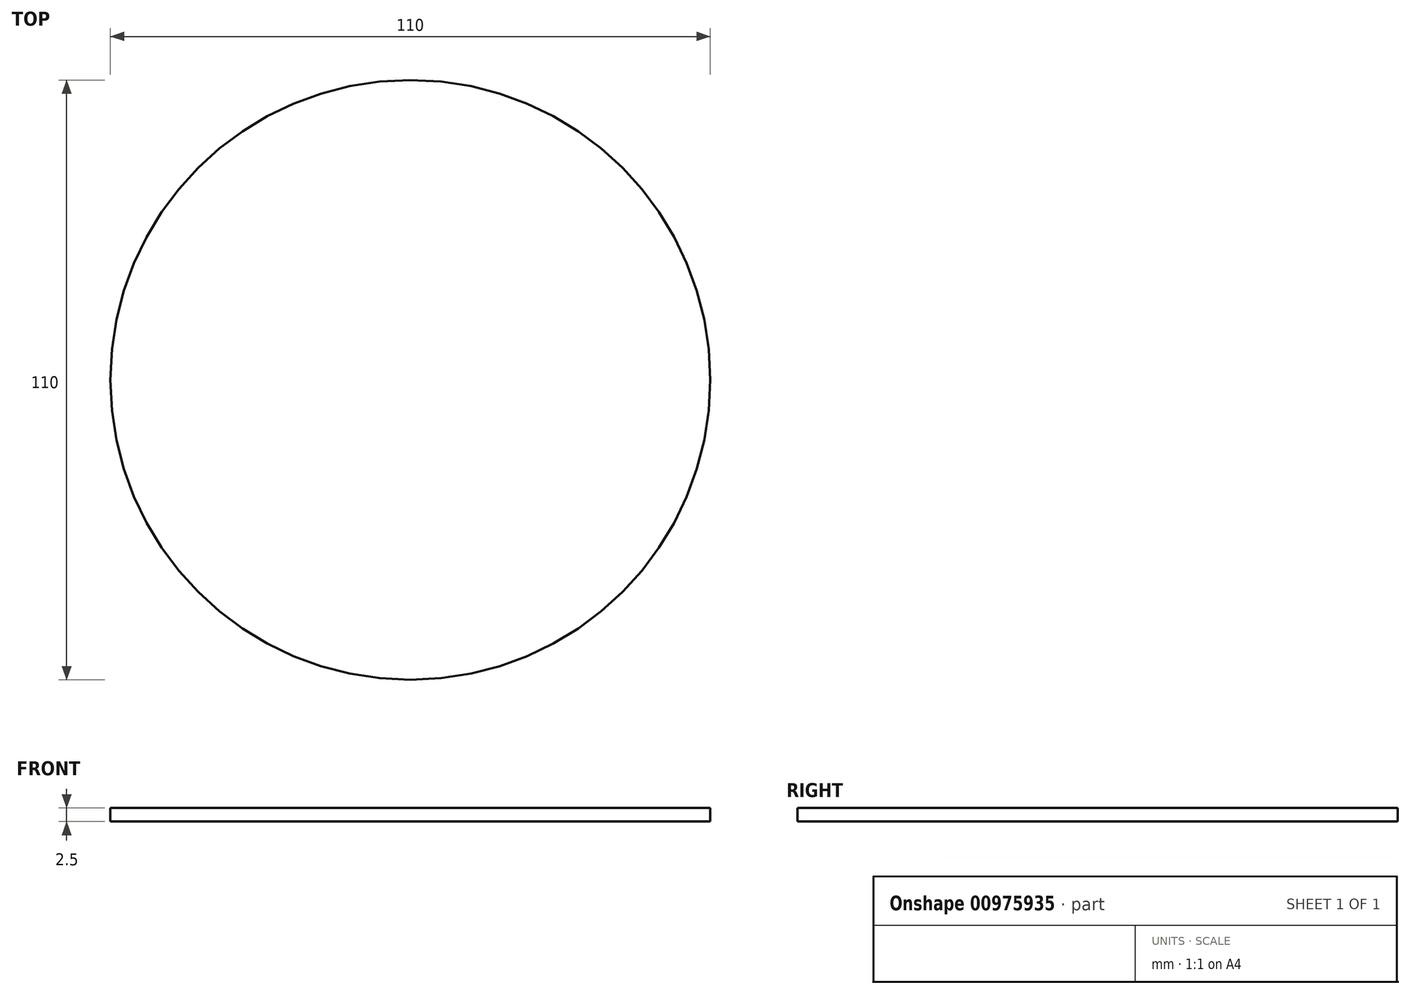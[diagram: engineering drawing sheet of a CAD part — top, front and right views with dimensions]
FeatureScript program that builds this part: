
annotation { "Feature Type Name" : "Feature", "Feature Type Description" : "" }
export const myFeature = defineFeature(function(context is Context, id is Id, definition is map)
    precondition{}
    {
        {
            var Q0;
            Q0=qCreatedBy(makeId("Top.planeOp"),FACE);
            var sketch = newSketch(context, id + "F0", { "sketchPlane" : qUnion([Q0])});
            skCircle(sketch, "E0", {"center": v(0, 0) * mm, "radius": 55 * mm});
            skSolve(sketch);
        }
        {
            var Q0;
            Q0 = qSketchRegion(id + "F0", true);
            extrude(context, id + "F1", {"entities" : qUnion([Q0]), "depth" : 2.5 * mm, "offsetDistance" : 25 * mm});
        }
    });
